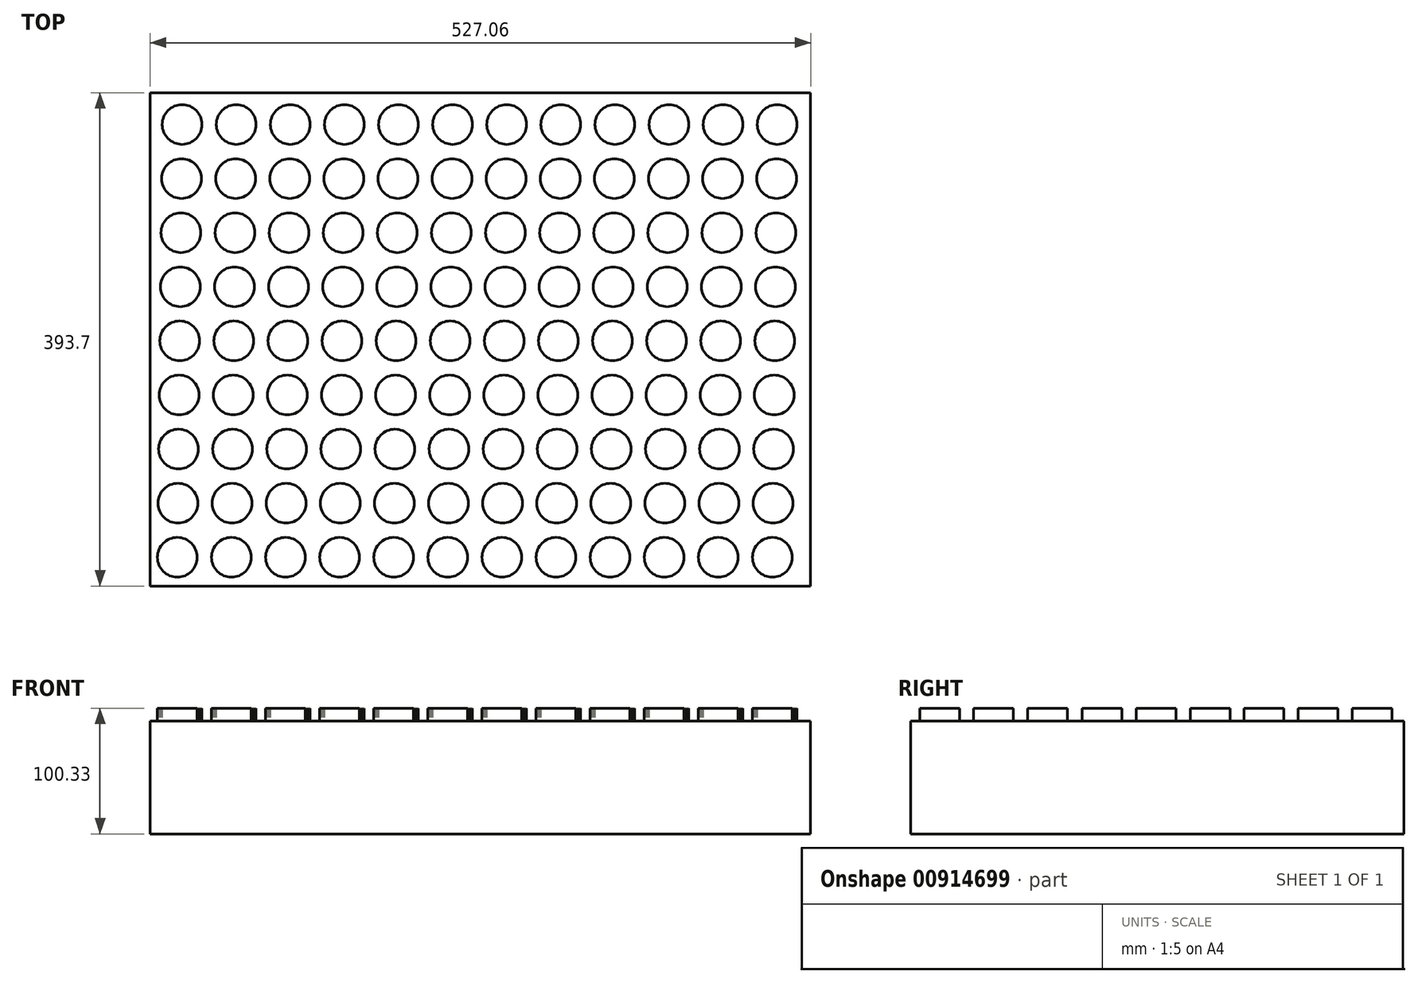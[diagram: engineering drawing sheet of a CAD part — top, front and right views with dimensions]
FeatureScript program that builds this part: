
annotation { "Feature Type Name" : "Feature", "Feature Type Description" : "" }
export const myFeature = defineFeature(function(context is Context, id is Id, definition is map)
    precondition{}
    {
        {
            var Q0;
            Q0=qCreatedBy(makeId("Top.planeOp"),FACE);
            var sketch = newSketch(context, id + "F0", { "sketchPlane" : qUnion([Q0])});
            skLineSegment(sketch, "E0.bottom", {"start": v(-263.53, 196.85) * mm, "end": v(263.53, 196.85) * mm});
            skLineSegment(sketch, "E0.top", {"start": v(-263.53, -196.85) * mm, "end": v(263.53, -196.85) * mm});
            skLineSegment(sketch, "E0.left", {"start": v(-263.53, 196.85) * mm, "end": v(-263.53, -196.85) * mm});
            skLineSegment(sketch, "E0.right", {"start": v(263.53, 196.85) * mm, "end": v(263.53, -196.85) * mm});
            skSolve(sketch);
        }
        {
            var Q0;
            Q0=makeQuery(id+"F0.imprint","IMPRINT",FACE,{"disambiguationData":[TD([[makeQuery(id+"F0.imprint","IMPRINT",EDGE,{"derivedFrom":sQuery(id+"F0.wireOp",EDGE,"E0.bottom")}),-1.0]])]});
            extrude(context, id + "F1", {"entities" : qUnion([Q0]), "depth" : 90.17 * mm, "offsetDistance" : 25.4 * mm});
        }
        {
            var Q0;
            Q0=makeQuery(id+"F1.opExtrude","CAP_FACE",FACE,{"disambiguationData":[OSD([sQuery(id+"F0.wireOp",EDGE,"E0.bottom"),sQuery(id+"F0.wireOp",EDGE,"E0.top"),sQuery(id+"F0.wireOp",EDGE,"E0.left"),sQuery(id+"F0.wireOp",EDGE,"E0.right")])],"isStart":false});
            var sketch = newSketch(context, id + "F2", { "sketchPlane" : qUnion([Q0])});
            skCircle(sketch, "E1", {"center": v(-238.13, 171.45) * mm, "radius": 15.88 * mm});
            skCircle(sketch, "E2.0.1.0", {"center": v(-238.6, 128.27) * mm, "radius": 15.88 * mm});
            skCircle(sketch, "E2.0.2.0", {"center": v(-239.08, 85.1) * mm, "radius": 15.88 * mm});
            skCircle(sketch, "E2.0.3.0", {"center": v(-239.56, 41.92) * mm, "radius": 15.88 * mm});
            skCircle(sketch, "E2.0.4.0", {"center": v(-240.04, -1.26) * mm, "radius": 15.88 * mm});
            skCircle(sketch, "E2.0.5.0", {"center": v(-240.52, -44.44) * mm, "radius": 15.88 * mm});
            skCircle(sketch, "E2.0.6.0", {"center": v(-241, -87.61) * mm, "radius": 15.88 * mm});
            skCircle(sketch, "E2.0.7.0", {"center": v(-241.48, -130.8) * mm, "radius": 15.88 * mm});
            skCircle(sketch, "E2.0.8.0", {"center": v(-241.96, -173.97) * mm, "radius": 15.88 * mm});
            skCircle(sketch, "E2.1.0.0", {"center": v(-194.95, 171.45) * mm, "radius": 15.88 * mm});
            skCircle(sketch, "E2.1.1.0", {"center": v(-195.42, 128.27) * mm, "radius": 15.88 * mm});
            skCircle(sketch, "E2.1.2.0", {"center": v(-195.9, 85.1) * mm, "radius": 15.88 * mm});
            skCircle(sketch, "E2.1.3.0", {"center": v(-196.38, 41.92) * mm, "radius": 15.88 * mm});
            skCircle(sketch, "E2.1.4.0", {"center": v(-196.86, -1.26) * mm, "radius": 15.88 * mm});
            skCircle(sketch, "E2.1.5.0", {"center": v(-197.34, -44.44) * mm, "radius": 15.88 * mm});
            skCircle(sketch, "E2.1.6.0", {"center": v(-197.82, -87.61) * mm, "radius": 15.88 * mm});
            skCircle(sketch, "E2.1.7.0", {"center": v(-198.3, -130.8) * mm, "radius": 15.88 * mm});
            skCircle(sketch, "E2.1.8.0", {"center": v(-198.78, -173.97) * mm, "radius": 15.88 * mm});
            skCircle(sketch, "E2.2.0.0", {"center": v(-151.77, 171.45) * mm, "radius": 15.88 * mm});
            skCircle(sketch, "E2.2.1.0", {"center": v(-152.24, 128.27) * mm, "radius": 15.88 * mm});
            skCircle(sketch, "E2.2.2.0", {"center": v(-152.72, 85.1) * mm, "radius": 15.88 * mm});
            skCircle(sketch, "E2.2.3.0", {"center": v(-153.2, 41.92) * mm, "radius": 15.88 * mm});
            skCircle(sketch, "E2.2.4.0", {"center": v(-153.68, -1.26) * mm, "radius": 15.88 * mm});
            skCircle(sketch, "E2.2.5.0", {"center": v(-154.16, -44.44) * mm, "radius": 15.88 * mm});
            skCircle(sketch, "E2.2.6.0", {"center": v(-154.64, -87.61) * mm, "radius": 15.88 * mm});
            skCircle(sketch, "E2.2.7.0", {"center": v(-155.12, -130.8) * mm, "radius": 15.88 * mm});
            skCircle(sketch, "E2.2.8.0", {"center": v(-155.6, -173.97) * mm, "radius": 15.88 * mm});
            skCircle(sketch, "E2.3.0.0", {"center": v(-108.59, 171.45) * mm, "radius": 15.88 * mm});
            skCircle(sketch, "E2.3.1.0", {"center": v(-109.06, 128.27) * mm, "radius": 15.88 * mm});
            skCircle(sketch, "E2.3.2.0", {"center": v(-109.54, 85.1) * mm, "radius": 15.88 * mm});
            skCircle(sketch, "E2.3.3.0", {"center": v(-110.02, 41.92) * mm, "radius": 15.88 * mm});
            skCircle(sketch, "E2.3.4.0", {"center": v(-110.5, -1.26) * mm, "radius": 15.88 * mm});
            skCircle(sketch, "E2.3.5.0", {"center": v(-110.98, -44.44) * mm, "radius": 15.88 * mm});
            skCircle(sketch, "E2.3.6.0", {"center": v(-111.46, -87.61) * mm, "radius": 15.88 * mm});
            skCircle(sketch, "E2.3.7.0", {"center": v(-111.94, -130.8) * mm, "radius": 15.88 * mm});
            skCircle(sketch, "E2.3.8.0", {"center": v(-112.42, -173.97) * mm, "radius": 15.88 * mm});
            skCircle(sketch, "E2.4.0.0", {"center": v(-65.4, 171.45) * mm, "radius": 15.88 * mm});
            skCircle(sketch, "E2.4.1.0", {"center": v(-65.88, 128.27) * mm, "radius": 15.88 * mm});
            skCircle(sketch, "E2.4.2.0", {"center": v(-66.36, 85.1) * mm, "radius": 15.88 * mm});
            skCircle(sketch, "E2.4.3.0", {"center": v(-66.84, 41.92) * mm, "radius": 15.88 * mm});
            skCircle(sketch, "E2.4.4.0", {"center": v(-67.32, -1.26) * mm, "radius": 15.88 * mm});
            skCircle(sketch, "E2.4.5.0", {"center": v(-67.8, -44.44) * mm, "radius": 15.88 * mm});
            skCircle(sketch, "E2.4.6.0", {"center": v(-68.28, -87.61) * mm, "radius": 15.88 * mm});
            skCircle(sketch, "E2.4.7.0", {"center": v(-68.76, -130.8) * mm, "radius": 15.88 * mm});
            skCircle(sketch, "E2.4.8.0", {"center": v(-69.24, -173.97) * mm, "radius": 15.88 * mm});
            skCircle(sketch, "E2.5.0.0", {"center": v(-22.23, 171.45) * mm, "radius": 15.88 * mm});
            skCircle(sketch, "E2.5.1.0", {"center": v(-22.7, 128.27) * mm, "radius": 15.88 * mm});
            skCircle(sketch, "E2.5.2.0", {"center": v(-23.18, 85.1) * mm, "radius": 15.88 * mm});
            skCircle(sketch, "E2.5.3.0", {"center": v(-23.66, 41.92) * mm, "radius": 15.88 * mm});
            skCircle(sketch, "E2.5.4.0", {"center": v(-24.14, -1.26) * mm, "radius": 15.88 * mm});
            skCircle(sketch, "E2.5.5.0", {"center": v(-24.62, -44.44) * mm, "radius": 15.88 * mm});
            skCircle(sketch, "E2.5.6.0", {"center": v(-25.1, -87.61) * mm, "radius": 15.88 * mm});
            skCircle(sketch, "E2.5.7.0", {"center": v(-25.58, -130.8) * mm, "radius": 15.88 * mm});
            skCircle(sketch, "E2.5.8.0", {"center": v(-26.06, -173.97) * mm, "radius": 15.88 * mm});
            skCircle(sketch, "E2.6.0.0", {"center": v(20.95, 171.45) * mm, "radius": 15.88 * mm});
            skCircle(sketch, "E2.6.1.0", {"center": v(20.48, 128.27) * mm, "radius": 15.88 * mm});
            skCircle(sketch, "E2.6.2.0", {"center": v(20, 85.1) * mm, "radius": 15.88 * mm});
            skCircle(sketch, "E2.6.3.0", {"center": v(19.52, 41.92) * mm, "radius": 15.88 * mm});
            skCircle(sketch, "E2.6.4.0", {"center": v(19.04, -1.26) * mm, "radius": 15.88 * mm});
            skCircle(sketch, "E2.6.5.0", {"center": v(18.56, -44.44) * mm, "radius": 15.88 * mm});
            skCircle(sketch, "E2.6.6.0", {"center": v(18.08, -87.61) * mm, "radius": 15.88 * mm});
            skCircle(sketch, "E2.6.7.0", {"center": v(17.6, -130.8) * mm, "radius": 15.88 * mm});
            skCircle(sketch, "E2.6.8.0", {"center": v(17.12, -173.97) * mm, "radius": 15.88 * mm});
            skCircle(sketch, "E2.7.0.0", {"center": v(64.13, 171.45) * mm, "radius": 15.88 * mm});
            skCircle(sketch, "E2.7.1.0", {"center": v(63.66, 128.27) * mm, "radius": 15.88 * mm});
            skCircle(sketch, "E2.7.2.0", {"center": v(63.18, 85.1) * mm, "radius": 15.88 * mm});
            skCircle(sketch, "E2.7.3.0", {"center": v(62.7, 41.92) * mm, "radius": 15.88 * mm});
            skCircle(sketch, "E2.7.4.0", {"center": v(62.22, -1.26) * mm, "radius": 15.88 * mm});
            skCircle(sketch, "E2.7.5.0", {"center": v(61.74, -44.44) * mm, "radius": 15.88 * mm});
            skCircle(sketch, "E2.7.6.0", {"center": v(61.26, -87.61) * mm, "radius": 15.88 * mm});
            skCircle(sketch, "E2.7.7.0", {"center": v(60.78, -130.8) * mm, "radius": 15.88 * mm});
            skCircle(sketch, "E2.7.8.0", {"center": v(60.3, -173.97) * mm, "radius": 15.88 * mm});
            skCircle(sketch, "E2.8.0.0", {"center": v(107.31, 171.45) * mm, "radius": 15.88 * mm});
            skCircle(sketch, "E2.8.1.0", {"center": v(106.84, 128.27) * mm, "radius": 15.88 * mm});
            skCircle(sketch, "E2.8.2.0", {"center": v(106.36, 85.1) * mm, "radius": 15.88 * mm});
            skCircle(sketch, "E2.8.3.0", {"center": v(105.88, 41.92) * mm, "radius": 15.88 * mm});
            skCircle(sketch, "E2.8.4.0", {"center": v(105.4, -1.26) * mm, "radius": 15.88 * mm});
            skCircle(sketch, "E2.8.5.0", {"center": v(104.92, -44.44) * mm, "radius": 15.88 * mm});
            skCircle(sketch, "E2.8.6.0", {"center": v(104.44, -87.61) * mm, "radius": 15.88 * mm});
            skCircle(sketch, "E2.8.7.0", {"center": v(103.96, -130.8) * mm, "radius": 15.88 * mm});
            skCircle(sketch, "E2.8.8.0", {"center": v(103.48, -173.97) * mm, "radius": 15.88 * mm});
            skCircle(sketch, "E2.9.0.0", {"center": v(150.5, 171.45) * mm, "radius": 15.88 * mm});
            skCircle(sketch, "E2.9.1.0", {"center": v(150.02, 128.27) * mm, "radius": 15.88 * mm});
            skCircle(sketch, "E2.9.2.0", {"center": v(149.54, 85.1) * mm, "radius": 15.88 * mm});
            skCircle(sketch, "E2.9.3.0", {"center": v(149.06, 41.92) * mm, "radius": 15.88 * mm});
            skCircle(sketch, "E2.9.4.0", {"center": v(148.58, -1.26) * mm, "radius": 15.88 * mm});
            skCircle(sketch, "E2.9.5.0", {"center": v(148.1, -44.44) * mm, "radius": 15.88 * mm});
            skCircle(sketch, "E2.9.6.0", {"center": v(147.62, -87.61) * mm, "radius": 15.88 * mm});
            skCircle(sketch, "E2.9.7.0", {"center": v(147.14, -130.8) * mm, "radius": 15.88 * mm});
            skCircle(sketch, "E2.9.8.0", {"center": v(146.66, -173.97) * mm, "radius": 15.88 * mm});
            skCircle(sketch, "E2.10.0.0", {"center": v(193.67, 171.45) * mm, "radius": 15.88 * mm});
            skCircle(sketch, "E2.10.1.0", {"center": v(193.2, 128.27) * mm, "radius": 15.88 * mm});
            skCircle(sketch, "E2.10.2.0", {"center": v(192.72, 85.1) * mm, "radius": 15.88 * mm});
            skCircle(sketch, "E2.10.3.0", {"center": v(192.24, 41.92) * mm, "radius": 15.88 * mm});
            skCircle(sketch, "E2.10.4.0", {"center": v(191.76, -1.26) * mm, "radius": 15.88 * mm});
            skCircle(sketch, "E2.10.5.0", {"center": v(191.28, -44.44) * mm, "radius": 15.88 * mm});
            skCircle(sketch, "E2.10.6.0", {"center": v(190.8, -87.61) * mm, "radius": 15.88 * mm});
            skCircle(sketch, "E2.10.7.0", {"center": v(190.32, -130.8) * mm, "radius": 15.88 * mm});
            skCircle(sketch, "E2.10.8.0", {"center": v(189.84, -173.97) * mm, "radius": 15.88 * mm});
            skCircle(sketch, "E2.11.0.0", {"center": v(236.85, 171.45) * mm, "radius": 15.88 * mm});
            skCircle(sketch, "E2.11.1.0", {"center": v(236.38, 128.27) * mm, "radius": 15.88 * mm});
            skCircle(sketch, "E2.11.2.0", {"center": v(235.9, 85.1) * mm, "radius": 15.88 * mm});
            skCircle(sketch, "E2.11.3.0", {"center": v(235.42, 41.92) * mm, "radius": 15.88 * mm});
            skCircle(sketch, "E2.11.4.0", {"center": v(234.94, -1.26) * mm, "radius": 15.88 * mm});
            skCircle(sketch, "E2.11.5.0", {"center": v(234.46, -44.44) * mm, "radius": 15.88 * mm});
            skCircle(sketch, "E2.11.6.0", {"center": v(233.98, -87.61) * mm, "radius": 15.88 * mm});
            skCircle(sketch, "E2.11.7.0", {"center": v(233.5, -130.8) * mm, "radius": 15.88 * mm});
            skCircle(sketch, "E2.11.8.0", {"center": v(233.02, -173.97) * mm, "radius": 15.88 * mm});
            skLineSegment(sketch, "E2.direction1", {"start": v(-238.13, 171.45) * mm, "end": v(-194.95, 171.45) * mm, "construction": true});
            skLineSegment(sketch, "E2.direction2", {"start": v(-238.13, 171.45) * mm, "end": v(-238.6, 128.27) * mm, "construction": true});
            skSolve(sketch);
        }
        {
            var Q0;
            Q0=makeQuery(id+"F2.imprint","IMPRINT",FACE,{"disambiguationData":[TD([[makeQuery(id+"F2.imprint","IMPRINT",EDGE,{"derivedFrom":sQuery(id+"F2.wireOp",EDGE,"E1")}),1.0]])]});
            var Q1;
            Q1=makeQuery(id+"F2.imprint","IMPRINT",FACE,{"disambiguationData":[TD([[makeQuery(id+"F2.imprint","IMPRINT",EDGE,{"derivedFrom":sQuery(id+"F2.wireOp",EDGE,"E2.1.0.0")}),1.0]])]});
            var Q2;
            Q2=makeQuery(id+"F2.imprint","IMPRINT",FACE,{"disambiguationData":[TD([[makeQuery(id+"F2.imprint","IMPRINT",EDGE,{"derivedFrom":sQuery(id+"F2.wireOp",EDGE,"E2.2.0.0")}),1.0]])]});
            var Q3;
            Q3=makeQuery(id+"F2.imprint","IMPRINT",FACE,{"disambiguationData":[TD([[makeQuery(id+"F2.imprint","IMPRINT",EDGE,{"derivedFrom":sQuery(id+"F2.wireOp",EDGE,"E2.3.0.0")}),1.0]])]});
            var Q4;
            Q4=makeQuery(id+"F2.imprint","IMPRINT",FACE,{"disambiguationData":[TD([[makeQuery(id+"F2.imprint","IMPRINT",EDGE,{"derivedFrom":sQuery(id+"F2.wireOp",EDGE,"E2.4.0.0")}),1.0]])]});
            var Q5;
            Q5=makeQuery(id+"F2.imprint","IMPRINT",FACE,{"disambiguationData":[TD([[makeQuery(id+"F2.imprint","IMPRINT",EDGE,{"derivedFrom":sQuery(id+"F2.wireOp",EDGE,"E2.5.0.0")}),1.0]])]});
            var Q6;
            Q6=makeQuery(id+"F2.imprint","IMPRINT",FACE,{"disambiguationData":[TD([[makeQuery(id+"F2.imprint","IMPRINT",EDGE,{"derivedFrom":sQuery(id+"F2.wireOp",EDGE,"E2.6.0.0")}),1.0]])]});
            var Q7;
            Q7=makeQuery(id+"F2.imprint","IMPRINT",FACE,{"disambiguationData":[TD([[makeQuery(id+"F2.imprint","IMPRINT",EDGE,{"derivedFrom":sQuery(id+"F2.wireOp",EDGE,"E2.7.0.0")}),1.0]])]});
            var Q8;
            Q8=makeQuery(id+"F2.imprint","IMPRINT",FACE,{"disambiguationData":[TD([[makeQuery(id+"F2.imprint","IMPRINT",EDGE,{"derivedFrom":sQuery(id+"F2.wireOp",EDGE,"E2.8.0.0")}),1.0]])]});
            var Q9;
            Q9=makeQuery(id+"F2.imprint","IMPRINT",FACE,{"disambiguationData":[TD([[makeQuery(id+"F2.imprint","IMPRINT",EDGE,{"derivedFrom":sQuery(id+"F2.wireOp",EDGE,"E2.9.0.0")}),1.0]])]});
            var Q10;
            Q10=makeQuery(id+"F2.imprint","IMPRINT",FACE,{"disambiguationData":[TD([[makeQuery(id+"F2.imprint","IMPRINT",EDGE,{"derivedFrom":sQuery(id+"F2.wireOp",EDGE,"E2.10.0.0")}),1.0]])]});
            var Q11;
            Q11=makeQuery(id+"F2.imprint","IMPRINT",FACE,{"disambiguationData":[TD([[makeQuery(id+"F2.imprint","IMPRINT",EDGE,{"derivedFrom":sQuery(id+"F2.wireOp",EDGE,"E2.11.0.0")}),1.0]])]});
            var Q12;
            Q12=makeQuery(id+"F2.imprint","IMPRINT",FACE,{"disambiguationData":[TD([[makeQuery(id+"F2.imprint","IMPRINT",EDGE,{"derivedFrom":sQuery(id+"F2.wireOp",EDGE,"E2.11.1.0")}),1.0]])]});
            var Q13;
            Q13=makeQuery(id+"F2.imprint","IMPRINT",FACE,{"disambiguationData":[TD([[makeQuery(id+"F2.imprint","IMPRINT",EDGE,{"derivedFrom":sQuery(id+"F2.wireOp",EDGE,"E2.10.1.0")}),1.0]])]});
            var Q14;
            Q14=makeQuery(id+"F2.imprint","IMPRINT",FACE,{"disambiguationData":[TD([[makeQuery(id+"F2.imprint","IMPRINT",EDGE,{"derivedFrom":sQuery(id+"F2.wireOp",EDGE,"E2.9.1.0")}),1.0]])]});
            var Q15;
            Q15=makeQuery(id+"F2.imprint","IMPRINT",FACE,{"disambiguationData":[TD([[makeQuery(id+"F2.imprint","IMPRINT",EDGE,{"derivedFrom":sQuery(id+"F2.wireOp",EDGE,"E2.8.1.0")}),1.0]])]});
            var Q16;
            Q16=makeQuery(id+"F2.imprint","IMPRINT",FACE,{"disambiguationData":[TD([[makeQuery(id+"F2.imprint","IMPRINT",EDGE,{"derivedFrom":sQuery(id+"F2.wireOp",EDGE,"E2.7.1.0")}),1.0]])]});
            var Q17;
            Q17=makeQuery(id+"F2.imprint","IMPRINT",FACE,{"disambiguationData":[TD([[makeQuery(id+"F2.imprint","IMPRINT",EDGE,{"derivedFrom":sQuery(id+"F2.wireOp",EDGE,"E2.6.1.0")}),1.0]])]});
            var Q18;
            Q18=makeQuery(id+"F2.imprint","IMPRINT",FACE,{"disambiguationData":[TD([[makeQuery(id+"F2.imprint","IMPRINT",EDGE,{"derivedFrom":sQuery(id+"F2.wireOp",EDGE,"E2.5.1.0")}),1.0]])]});
            var Q19;
            Q19=makeQuery(id+"F2.imprint","IMPRINT",FACE,{"disambiguationData":[TD([[makeQuery(id+"F2.imprint","IMPRINT",EDGE,{"derivedFrom":sQuery(id+"F2.wireOp",EDGE,"E2.4.1.0")}),1.0]])]});
            var Q20;
            Q20=makeQuery(id+"F2.imprint","IMPRINT",FACE,{"disambiguationData":[TD([[makeQuery(id+"F2.imprint","IMPRINT",EDGE,{"derivedFrom":sQuery(id+"F2.wireOp",EDGE,"E2.3.1.0")}),1.0]])]});
            var Q21;
            Q21=makeQuery(id+"F2.imprint","IMPRINT",FACE,{"disambiguationData":[TD([[makeQuery(id+"F2.imprint","IMPRINT",EDGE,{"derivedFrom":sQuery(id+"F2.wireOp",EDGE,"E2.2.1.0")}),1.0]])]});
            var Q22;
            Q22=makeQuery(id+"F2.imprint","IMPRINT",FACE,{"disambiguationData":[TD([[makeQuery(id+"F2.imprint","IMPRINT",EDGE,{"derivedFrom":sQuery(id+"F2.wireOp",EDGE,"E2.1.1.0")}),1.0]])]});
            var Q23;
            Q23=makeQuery(id+"F2.imprint","IMPRINT",FACE,{"disambiguationData":[TD([[makeQuery(id+"F2.imprint","IMPRINT",EDGE,{"derivedFrom":sQuery(id+"F2.wireOp",EDGE,"E2.0.1.0")}),1.0]])]});
            var Q24;
            Q24=makeQuery(id+"F2.imprint","IMPRINT",FACE,{"disambiguationData":[TD([[makeQuery(id+"F2.imprint","IMPRINT",EDGE,{"derivedFrom":sQuery(id+"F2.wireOp",EDGE,"E2.0.2.0")}),1.0]])]});
            var Q25;
            Q25=makeQuery(id+"F2.imprint","IMPRINT",FACE,{"disambiguationData":[TD([[makeQuery(id+"F2.imprint","IMPRINT",EDGE,{"derivedFrom":sQuery(id+"F2.wireOp",EDGE,"E2.1.2.0")}),1.0]])]});
            var Q26;
            Q26=makeQuery(id+"F2.imprint","IMPRINT",FACE,{"disambiguationData":[TD([[makeQuery(id+"F2.imprint","IMPRINT",EDGE,{"derivedFrom":sQuery(id+"F2.wireOp",EDGE,"E2.2.2.0")}),1.0]])]});
            var Q27;
            Q27=makeQuery(id+"F2.imprint","IMPRINT",FACE,{"disambiguationData":[TD([[makeQuery(id+"F2.imprint","IMPRINT",EDGE,{"derivedFrom":sQuery(id+"F2.wireOp",EDGE,"E2.3.2.0")}),1.0]])]});
            var Q28;
            Q28=makeQuery(id+"F2.imprint","IMPRINT",FACE,{"disambiguationData":[TD([[makeQuery(id+"F2.imprint","IMPRINT",EDGE,{"derivedFrom":sQuery(id+"F2.wireOp",EDGE,"E2.4.2.0")}),1.0]])]});
            var Q29;
            Q29=makeQuery(id+"F2.imprint","IMPRINT",FACE,{"disambiguationData":[TD([[makeQuery(id+"F2.imprint","IMPRINT",EDGE,{"derivedFrom":sQuery(id+"F2.wireOp",EDGE,"E2.5.2.0")}),1.0]])]});
            var Q30;
            Q30=makeQuery(id+"F2.imprint","IMPRINT",FACE,{"disambiguationData":[TD([[makeQuery(id+"F2.imprint","IMPRINT",EDGE,{"derivedFrom":sQuery(id+"F2.wireOp",EDGE,"E2.6.2.0")}),1.0]])]});
            var Q31;
            Q31=makeQuery(id+"F2.imprint","IMPRINT",FACE,{"disambiguationData":[TD([[makeQuery(id+"F2.imprint","IMPRINT",EDGE,{"derivedFrom":sQuery(id+"F2.wireOp",EDGE,"E2.7.2.0")}),1.0]])]});
            var Q32;
            Q32=makeQuery(id+"F2.imprint","IMPRINT",FACE,{"disambiguationData":[TD([[makeQuery(id+"F2.imprint","IMPRINT",EDGE,{"derivedFrom":sQuery(id+"F2.wireOp",EDGE,"E2.8.2.0")}),1.0]])]});
            var Q33;
            Q33=makeQuery(id+"F2.imprint","IMPRINT",FACE,{"disambiguationData":[TD([[makeQuery(id+"F2.imprint","IMPRINT",EDGE,{"derivedFrom":sQuery(id+"F2.wireOp",EDGE,"E2.9.2.0")}),1.0]])]});
            var Q34;
            Q34=makeQuery(id+"F2.imprint","IMPRINT",FACE,{"disambiguationData":[TD([[makeQuery(id+"F2.imprint","IMPRINT",EDGE,{"derivedFrom":sQuery(id+"F2.wireOp",EDGE,"E2.10.2.0")}),1.0]])]});
            var Q35;
            Q35=makeQuery(id+"F2.imprint","IMPRINT",FACE,{"disambiguationData":[TD([[makeQuery(id+"F2.imprint","IMPRINT",EDGE,{"derivedFrom":sQuery(id+"F2.wireOp",EDGE,"E2.11.2.0")}),1.0]])]});
            var Q36;
            Q36=makeQuery(id+"F2.imprint","IMPRINT",FACE,{"disambiguationData":[TD([[makeQuery(id+"F2.imprint","IMPRINT",EDGE,{"derivedFrom":sQuery(id+"F2.wireOp",EDGE,"E2.11.3.0")}),1.0]])]});
            var Q37;
            Q37=makeQuery(id+"F2.imprint","IMPRINT",FACE,{"disambiguationData":[TD([[makeQuery(id+"F2.imprint","IMPRINT",EDGE,{"derivedFrom":sQuery(id+"F2.wireOp",EDGE,"E2.10.3.0")}),1.0]])]});
            var Q38;
            Q38=makeQuery(id+"F2.imprint","IMPRINT",FACE,{"disambiguationData":[TD([[makeQuery(id+"F2.imprint","IMPRINT",EDGE,{"derivedFrom":sQuery(id+"F2.wireOp",EDGE,"E2.9.3.0")}),1.0]])]});
            var Q39;
            Q39=makeQuery(id+"F2.imprint","IMPRINT",FACE,{"disambiguationData":[TD([[makeQuery(id+"F2.imprint","IMPRINT",EDGE,{"derivedFrom":sQuery(id+"F2.wireOp",EDGE,"E2.8.3.0")}),1.0]])]});
            var Q40;
            Q40=makeQuery(id+"F2.imprint","IMPRINT",FACE,{"disambiguationData":[TD([[makeQuery(id+"F2.imprint","IMPRINT",EDGE,{"derivedFrom":sQuery(id+"F2.wireOp",EDGE,"E2.7.3.0")}),1.0]])]});
            var Q41;
            Q41=makeQuery(id+"F2.imprint","IMPRINT",FACE,{"disambiguationData":[TD([[makeQuery(id+"F2.imprint","IMPRINT",EDGE,{"derivedFrom":sQuery(id+"F2.wireOp",EDGE,"E2.6.3.0")}),1.0]])]});
            var Q42;
            Q42=makeQuery(id+"F2.imprint","IMPRINT",FACE,{"disambiguationData":[TD([[makeQuery(id+"F2.imprint","IMPRINT",EDGE,{"derivedFrom":sQuery(id+"F2.wireOp",EDGE,"E2.5.3.0")}),1.0]])]});
            var Q43;
            Q43=makeQuery(id+"F2.imprint","IMPRINT",FACE,{"disambiguationData":[TD([[makeQuery(id+"F2.imprint","IMPRINT",EDGE,{"derivedFrom":sQuery(id+"F2.wireOp",EDGE,"E2.4.3.0")}),1.0]])]});
            var Q44;
            Q44=makeQuery(id+"F2.imprint","IMPRINT",FACE,{"disambiguationData":[TD([[makeQuery(id+"F2.imprint","IMPRINT",EDGE,{"derivedFrom":sQuery(id+"F2.wireOp",EDGE,"E2.3.3.0")}),1.0]])]});
            var Q45;
            Q45=makeQuery(id+"F2.imprint","IMPRINT",FACE,{"disambiguationData":[TD([[makeQuery(id+"F2.imprint","IMPRINT",EDGE,{"derivedFrom":sQuery(id+"F2.wireOp",EDGE,"E2.2.3.0")}),1.0]])]});
            var Q46;
            Q46=makeQuery(id+"F2.imprint","IMPRINT",FACE,{"disambiguationData":[TD([[makeQuery(id+"F2.imprint","IMPRINT",EDGE,{"derivedFrom":sQuery(id+"F2.wireOp",EDGE,"E2.1.3.0")}),1.0]])]});
            var Q47;
            Q47=makeQuery(id+"F2.imprint","IMPRINT",FACE,{"disambiguationData":[TD([[makeQuery(id+"F2.imprint","IMPRINT",EDGE,{"derivedFrom":sQuery(id+"F2.wireOp",EDGE,"E2.0.3.0")}),1.0]])]});
            var Q48;
            Q48=makeQuery(id+"F2.imprint","IMPRINT",FACE,{"disambiguationData":[TD([[makeQuery(id+"F2.imprint","IMPRINT",EDGE,{"derivedFrom":sQuery(id+"F2.wireOp",EDGE,"E2.0.4.0")}),1.0]])]});
            var Q49;
            Q49=makeQuery(id+"F2.imprint","IMPRINT",FACE,{"disambiguationData":[TD([[makeQuery(id+"F2.imprint","IMPRINT",EDGE,{"derivedFrom":sQuery(id+"F2.wireOp",EDGE,"E2.0.5.0")}),1.0]])]});
            var Q50;
            Q50=makeQuery(id+"F2.imprint","IMPRINT",FACE,{"disambiguationData":[TD([[makeQuery(id+"F2.imprint","IMPRINT",EDGE,{"derivedFrom":sQuery(id+"F2.wireOp",EDGE,"E2.1.4.0")}),1.0]])]});
            var Q51;
            Q51=makeQuery(id+"F2.imprint","IMPRINT",FACE,{"disambiguationData":[TD([[makeQuery(id+"F2.imprint","IMPRINT",EDGE,{"derivedFrom":sQuery(id+"F2.wireOp",EDGE,"E2.1.5.0")}),1.0]])]});
            var Q52;
            Q52=makeQuery(id+"F2.imprint","IMPRINT",FACE,{"disambiguationData":[TD([[makeQuery(id+"F2.imprint","IMPRINT",EDGE,{"derivedFrom":sQuery(id+"F2.wireOp",EDGE,"E2.2.4.0")}),1.0]])]});
            var Q53;
            Q53=makeQuery(id+"F2.imprint","IMPRINT",FACE,{"disambiguationData":[TD([[makeQuery(id+"F2.imprint","IMPRINT",EDGE,{"derivedFrom":sQuery(id+"F2.wireOp",EDGE,"E2.2.5.0")}),1.0]])]});
            var Q54;
            Q54=makeQuery(id+"F2.imprint","IMPRINT",FACE,{"disambiguationData":[TD([[makeQuery(id+"F2.imprint","IMPRINT",EDGE,{"derivedFrom":sQuery(id+"F2.wireOp",EDGE,"E2.3.4.0")}),1.0]])]});
            var Q55;
            Q55=makeQuery(id+"F2.imprint","IMPRINT",FACE,{"disambiguationData":[TD([[makeQuery(id+"F2.imprint","IMPRINT",EDGE,{"derivedFrom":sQuery(id+"F2.wireOp",EDGE,"E2.3.5.0")}),1.0]])]});
            var Q56;
            Q56=makeQuery(id+"F2.imprint","IMPRINT",FACE,{"disambiguationData":[TD([[makeQuery(id+"F2.imprint","IMPRINT",EDGE,{"derivedFrom":sQuery(id+"F2.wireOp",EDGE,"E2.4.4.0")}),1.0]])]});
            var Q57;
            Q57=makeQuery(id+"F2.imprint","IMPRINT",FACE,{"disambiguationData":[TD([[makeQuery(id+"F2.imprint","IMPRINT",EDGE,{"derivedFrom":sQuery(id+"F2.wireOp",EDGE,"E2.4.5.0")}),1.0]])]});
            var Q58;
            Q58=makeQuery(id+"F2.imprint","IMPRINT",FACE,{"disambiguationData":[TD([[makeQuery(id+"F2.imprint","IMPRINT",EDGE,{"derivedFrom":sQuery(id+"F2.wireOp",EDGE,"E2.5.4.0")}),1.0]])]});
            var Q59;
            Q59=makeQuery(id+"F2.imprint","IMPRINT",FACE,{"disambiguationData":[TD([[makeQuery(id+"F2.imprint","IMPRINT",EDGE,{"derivedFrom":sQuery(id+"F2.wireOp",EDGE,"E2.5.5.0")}),1.0]])]});
            var Q60;
            Q60=makeQuery(id+"F2.imprint","IMPRINT",FACE,{"disambiguationData":[TD([[makeQuery(id+"F2.imprint","IMPRINT",EDGE,{"derivedFrom":sQuery(id+"F2.wireOp",EDGE,"E2.6.4.0")}),1.0]])]});
            var Q61;
            Q61=makeQuery(id+"F2.imprint","IMPRINT",FACE,{"disambiguationData":[TD([[makeQuery(id+"F2.imprint","IMPRINT",EDGE,{"derivedFrom":sQuery(id+"F2.wireOp",EDGE,"E2.6.5.0")}),1.0]])]});
            var Q62;
            Q62=makeQuery(id+"F2.imprint","IMPRINT",FACE,{"disambiguationData":[TD([[makeQuery(id+"F2.imprint","IMPRINT",EDGE,{"derivedFrom":sQuery(id+"F2.wireOp",EDGE,"E2.7.4.0")}),1.0]])]});
            var Q63;
            Q63=makeQuery(id+"F2.imprint","IMPRINT",FACE,{"disambiguationData":[TD([[makeQuery(id+"F2.imprint","IMPRINT",EDGE,{"derivedFrom":sQuery(id+"F2.wireOp",EDGE,"E2.7.5.0")}),1.0]])]});
            var Q64;
            Q64=makeQuery(id+"F2.imprint","IMPRINT",FACE,{"disambiguationData":[TD([[makeQuery(id+"F2.imprint","IMPRINT",EDGE,{"derivedFrom":sQuery(id+"F2.wireOp",EDGE,"E2.8.4.0")}),1.0]])]});
            var Q65;
            Q65=makeQuery(id+"F2.imprint","IMPRINT",FACE,{"disambiguationData":[TD([[makeQuery(id+"F2.imprint","IMPRINT",EDGE,{"derivedFrom":sQuery(id+"F2.wireOp",EDGE,"E2.8.5.0")}),1.0]])]});
            var Q66;
            Q66=makeQuery(id+"F2.imprint","IMPRINT",FACE,{"disambiguationData":[TD([[makeQuery(id+"F2.imprint","IMPRINT",EDGE,{"derivedFrom":sQuery(id+"F2.wireOp",EDGE,"E2.9.4.0")}),1.0]])]});
            var Q67;
            Q67=makeQuery(id+"F2.imprint","IMPRINT",FACE,{"disambiguationData":[TD([[makeQuery(id+"F2.imprint","IMPRINT",EDGE,{"derivedFrom":sQuery(id+"F2.wireOp",EDGE,"E2.9.5.0")}),1.0]])]});
            var Q68;
            Q68=makeQuery(id+"F2.imprint","IMPRINT",FACE,{"disambiguationData":[TD([[makeQuery(id+"F2.imprint","IMPRINT",EDGE,{"derivedFrom":sQuery(id+"F2.wireOp",EDGE,"E2.10.4.0")}),1.0]])]});
            var Q69;
            Q69=makeQuery(id+"F2.imprint","IMPRINT",FACE,{"disambiguationData":[TD([[makeQuery(id+"F2.imprint","IMPRINT",EDGE,{"derivedFrom":sQuery(id+"F2.wireOp",EDGE,"E2.10.5.0")}),1.0]])]});
            var Q70;
            Q70=makeQuery(id+"F2.imprint","IMPRINT",FACE,{"disambiguationData":[TD([[makeQuery(id+"F2.imprint","IMPRINT",EDGE,{"derivedFrom":sQuery(id+"F2.wireOp",EDGE,"E2.11.4.0")}),1.0]])]});
            var Q71;
            Q71=makeQuery(id+"F2.imprint","IMPRINT",FACE,{"disambiguationData":[TD([[makeQuery(id+"F2.imprint","IMPRINT",EDGE,{"derivedFrom":sQuery(id+"F2.wireOp",EDGE,"E2.11.5.0")}),1.0]])]});
            var Q72;
            Q72=makeQuery(id+"F2.imprint","IMPRINT",FACE,{"disambiguationData":[TD([[makeQuery(id+"F2.imprint","IMPRINT",EDGE,{"derivedFrom":sQuery(id+"F2.wireOp",EDGE,"E2.11.6.0")}),1.0]])]});
            var Q73;
            Q73=makeQuery(id+"F2.imprint","IMPRINT",FACE,{"disambiguationData":[TD([[makeQuery(id+"F2.imprint","IMPRINT",EDGE,{"derivedFrom":sQuery(id+"F2.wireOp",EDGE,"E2.11.7.0")}),1.0]])]});
            var Q74;
            Q74=makeQuery(id+"F2.imprint","IMPRINT",FACE,{"disambiguationData":[TD([[makeQuery(id+"F2.imprint","IMPRINT",EDGE,{"derivedFrom":sQuery(id+"F2.wireOp",EDGE,"E2.11.8.0")}),1.0]])]});
            var Q75;
            Q75=makeQuery(id+"F2.imprint","IMPRINT",FACE,{"disambiguationData":[TD([[makeQuery(id+"F2.imprint","IMPRINT",EDGE,{"derivedFrom":sQuery(id+"F2.wireOp",EDGE,"E2.10.8.0")}),1.0]])]});
            var Q76;
            Q76=makeQuery(id+"F2.imprint","IMPRINT",FACE,{"disambiguationData":[TD([[makeQuery(id+"F2.imprint","IMPRINT",EDGE,{"derivedFrom":sQuery(id+"F2.wireOp",EDGE,"E2.10.7.0")}),1.0]])]});
            var Q77;
            Q77=makeQuery(id+"F2.imprint","IMPRINT",FACE,{"disambiguationData":[TD([[makeQuery(id+"F2.imprint","IMPRINT",EDGE,{"derivedFrom":sQuery(id+"F2.wireOp",EDGE,"E2.10.6.0")}),1.0]])]});
            var Q78;
            Q78=makeQuery(id+"F2.imprint","IMPRINT",FACE,{"disambiguationData":[TD([[makeQuery(id+"F2.imprint","IMPRINT",EDGE,{"derivedFrom":sQuery(id+"F2.wireOp",EDGE,"E2.9.6.0")}),1.0]])]});
            var Q79;
            Q79=makeQuery(id+"F2.imprint","IMPRINT",FACE,{"disambiguationData":[TD([[makeQuery(id+"F2.imprint","IMPRINT",EDGE,{"derivedFrom":sQuery(id+"F2.wireOp",EDGE,"E2.9.7.0")}),1.0]])]});
            var Q80;
            Q80=makeQuery(id+"F2.imprint","IMPRINT",FACE,{"disambiguationData":[TD([[makeQuery(id+"F2.imprint","IMPRINT",EDGE,{"derivedFrom":sQuery(id+"F2.wireOp",EDGE,"E2.9.8.0")}),1.0]])]});
            var Q81;
            Q81=makeQuery(id+"F2.imprint","IMPRINT",FACE,{"disambiguationData":[TD([[makeQuery(id+"F2.imprint","IMPRINT",EDGE,{"derivedFrom":sQuery(id+"F2.wireOp",EDGE,"E2.8.8.0")}),1.0]])]});
            var Q82;
            Q82=makeQuery(id+"F2.imprint","IMPRINT",FACE,{"disambiguationData":[TD([[makeQuery(id+"F2.imprint","IMPRINT",EDGE,{"derivedFrom":sQuery(id+"F2.wireOp",EDGE,"E2.8.7.0")}),1.0]])]});
            var Q83;
            Q83=makeQuery(id+"F2.imprint","IMPRINT",FACE,{"disambiguationData":[TD([[makeQuery(id+"F2.imprint","IMPRINT",EDGE,{"derivedFrom":sQuery(id+"F2.wireOp",EDGE,"E2.8.6.0")}),1.0]])]});
            var Q84;
            Q84=makeQuery(id+"F2.imprint","IMPRINT",FACE,{"disambiguationData":[TD([[makeQuery(id+"F2.imprint","IMPRINT",EDGE,{"derivedFrom":sQuery(id+"F2.wireOp",EDGE,"E2.7.6.0")}),1.0]])]});
            var Q85;
            Q85=makeQuery(id+"F2.imprint","IMPRINT",FACE,{"disambiguationData":[TD([[makeQuery(id+"F2.imprint","IMPRINT",EDGE,{"derivedFrom":sQuery(id+"F2.wireOp",EDGE,"E2.7.7.0")}),1.0]])]});
            var Q86;
            Q86=makeQuery(id+"F2.imprint","IMPRINT",FACE,{"disambiguationData":[TD([[makeQuery(id+"F2.imprint","IMPRINT",EDGE,{"derivedFrom":sQuery(id+"F2.wireOp",EDGE,"E2.7.8.0")}),1.0]])]});
            var Q87;
            Q87=makeQuery(id+"F2.imprint","IMPRINT",FACE,{"disambiguationData":[TD([[makeQuery(id+"F2.imprint","IMPRINT",EDGE,{"derivedFrom":sQuery(id+"F2.wireOp",EDGE,"E2.6.8.0")}),1.0]])]});
            var Q88;
            Q88=makeQuery(id+"F2.imprint","IMPRINT",FACE,{"disambiguationData":[TD([[makeQuery(id+"F2.imprint","IMPRINT",EDGE,{"derivedFrom":sQuery(id+"F2.wireOp",EDGE,"E2.6.7.0")}),1.0]])]});
            var Q89;
            Q89=makeQuery(id+"F2.imprint","IMPRINT",FACE,{"disambiguationData":[TD([[makeQuery(id+"F2.imprint","IMPRINT",EDGE,{"derivedFrom":sQuery(id+"F2.wireOp",EDGE,"E2.6.6.0")}),1.0]])]});
            var Q90;
            Q90=makeQuery(id+"F2.imprint","IMPRINT",FACE,{"disambiguationData":[TD([[makeQuery(id+"F2.imprint","IMPRINT",EDGE,{"derivedFrom":sQuery(id+"F2.wireOp",EDGE,"E2.5.6.0")}),1.0]])]});
            var Q91;
            Q91=makeQuery(id+"F2.imprint","IMPRINT",FACE,{"disambiguationData":[TD([[makeQuery(id+"F2.imprint","IMPRINT",EDGE,{"derivedFrom":sQuery(id+"F2.wireOp",EDGE,"E2.5.7.0")}),1.0]])]});
            var Q92;
            Q92=makeQuery(id+"F2.imprint","IMPRINT",FACE,{"disambiguationData":[TD([[makeQuery(id+"F2.imprint","IMPRINT",EDGE,{"derivedFrom":sQuery(id+"F2.wireOp",EDGE,"E2.5.8.0")}),1.0]])]});
            var Q93;
            Q93=makeQuery(id+"F2.imprint","IMPRINT",FACE,{"disambiguationData":[TD([[makeQuery(id+"F2.imprint","IMPRINT",EDGE,{"derivedFrom":sQuery(id+"F2.wireOp",EDGE,"E2.4.8.0")}),1.0]])]});
            var Q94;
            Q94=makeQuery(id+"F2.imprint","IMPRINT",FACE,{"disambiguationData":[TD([[makeQuery(id+"F2.imprint","IMPRINT",EDGE,{"derivedFrom":sQuery(id+"F2.wireOp",EDGE,"E2.4.7.0")}),1.0]])]});
            var Q95;
            Q95=makeQuery(id+"F2.imprint","IMPRINT",FACE,{"disambiguationData":[TD([[makeQuery(id+"F2.imprint","IMPRINT",EDGE,{"derivedFrom":sQuery(id+"F2.wireOp",EDGE,"E2.4.6.0")}),1.0]])]});
            var Q96;
            Q96=makeQuery(id+"F2.imprint","IMPRINT",FACE,{"disambiguationData":[TD([[makeQuery(id+"F2.imprint","IMPRINT",EDGE,{"derivedFrom":sQuery(id+"F2.wireOp",EDGE,"E2.3.6.0")}),1.0]])]});
            var Q97;
            Q97=makeQuery(id+"F2.imprint","IMPRINT",FACE,{"disambiguationData":[TD([[makeQuery(id+"F2.imprint","IMPRINT",EDGE,{"derivedFrom":sQuery(id+"F2.wireOp",EDGE,"E2.3.7.0")}),1.0]])]});
            var Q98;
            Q98=makeQuery(id+"F2.imprint","IMPRINT",FACE,{"disambiguationData":[TD([[makeQuery(id+"F2.imprint","IMPRINT",EDGE,{"derivedFrom":sQuery(id+"F2.wireOp",EDGE,"E2.3.8.0")}),1.0]])]});
            var Q99;
            Q99=makeQuery(id+"F2.imprint","IMPRINT",FACE,{"disambiguationData":[TD([[makeQuery(id+"F2.imprint","IMPRINT",EDGE,{"derivedFrom":sQuery(id+"F2.wireOp",EDGE,"E2.2.8.0")}),1.0]])]});
            var Q100;
            Q100=makeQuery(id+"F2.imprint","IMPRINT",FACE,{"disambiguationData":[TD([[makeQuery(id+"F2.imprint","IMPRINT",EDGE,{"derivedFrom":sQuery(id+"F2.wireOp",EDGE,"E2.2.7.0")}),1.0]])]});
            var Q101;
            Q101=makeQuery(id+"F2.imprint","IMPRINT",FACE,{"disambiguationData":[TD([[makeQuery(id+"F2.imprint","IMPRINT",EDGE,{"derivedFrom":sQuery(id+"F2.wireOp",EDGE,"E2.2.6.0")}),1.0]])]});
            var Q102;
            Q102=makeQuery(id+"F2.imprint","IMPRINT",FACE,{"disambiguationData":[TD([[makeQuery(id+"F2.imprint","IMPRINT",EDGE,{"derivedFrom":sQuery(id+"F2.wireOp",EDGE,"E2.1.6.0")}),1.0]])]});
            var Q103;
            Q103=makeQuery(id+"F2.imprint","IMPRINT",FACE,{"disambiguationData":[TD([[makeQuery(id+"F2.imprint","IMPRINT",EDGE,{"derivedFrom":sQuery(id+"F2.wireOp",EDGE,"E2.1.7.0")}),1.0]])]});
            var Q104;
            Q104=makeQuery(id+"F2.imprint","IMPRINT",FACE,{"disambiguationData":[TD([[makeQuery(id+"F2.imprint","IMPRINT",EDGE,{"derivedFrom":sQuery(id+"F2.wireOp",EDGE,"E2.1.8.0")}),1.0]])]});
            var Q105;
            Q105=makeQuery(id+"F2.imprint","IMPRINT",FACE,{"disambiguationData":[TD([[makeQuery(id+"F2.imprint","IMPRINT",EDGE,{"derivedFrom":sQuery(id+"F2.wireOp",EDGE,"E2.0.8.0")}),1.0]])]});
            var Q106;
            Q106=makeQuery(id+"F2.imprint","IMPRINT",FACE,{"disambiguationData":[TD([[makeQuery(id+"F2.imprint","IMPRINT",EDGE,{"derivedFrom":sQuery(id+"F2.wireOp",EDGE,"E2.0.7.0")}),1.0]])]});
            var Q107;
            Q107=makeQuery(id+"F2.imprint","IMPRINT",FACE,{"disambiguationData":[TD([[makeQuery(id+"F2.imprint","IMPRINT",EDGE,{"derivedFrom":sQuery(id+"F2.wireOp",EDGE,"E2.0.6.0")}),1.0]])]});
            extrude(context, id + "F3", {"entities" : qUnion([Q0, Q1, Q2, Q3, Q4, Q5, Q6, Q7, Q8, Q9, Q10, Q11, Q12, Q13, Q14, Q15, Q16, Q17, Q18, Q19, Q20, Q21, Q22, Q23, Q24, Q25, Q26, Q27, Q28, Q29, Q30, Q31, Q32, Q33, Q34, Q35, Q36, Q37, Q38, Q39, Q40, Q41, Q42, Q43, Q44, Q45, Q46, Q47, Q48, Q49, Q50, Q51, Q52, Q53, Q54, Q55, Q56, Q57, Q58, Q59, Q60, Q61, Q62, Q63, Q64, Q65, Q66, Q67, Q68, Q69, Q70, Q71, Q72, Q73, Q74, Q75, Q76, Q77, Q78, Q79, Q80, Q81, Q82, Q83, Q84, Q85, Q86, Q87, Q88, Q89, Q90, Q91, Q92, Q93, Q94, Q95, Q96, Q97, Q98, Q99, Q100, Q101, Q102, Q103, Q104, Q105, Q106, Q107]), "operationType" : NewBodyOperationType.ADD, "depth" : 10.16 * mm, "offsetDistance" : 25.4 * mm});
        }
    });
